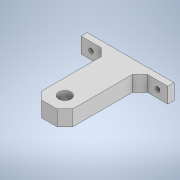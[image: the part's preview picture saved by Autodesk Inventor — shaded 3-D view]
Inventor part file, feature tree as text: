
AUTODESK INVENTOR PART (.ipt)
format: ipt  version: 2022 (Build 260153000, 153)  size: 274,432 bytes
history: native  units: mm
features: sketch x3, extrude x2, hole x2, other x1, chamfer x1
ambient origin geometry x8: Origin, YZ Plane, XZ Plane, XY Plane, X Axis, Y Axis, Z Axis, Center Point
bodies: Body1 (feature_tree)
feature tree (9):
  other  "Sólido1"
  sketch  "Esboço1"  dims[d0=56.0mm d1=10.0mm]
  extrude  "Extrusão1"  Depth=10.0mm
  extrude  "Extrusão2"  Depth=4.0mm TaperAngle=0.0deg
  chamfer  "Chanfro1"  Distance=52.426mm
  hole  "Furo1"  [1 undecoded]
  hole  "Furo2"  [1 undecoded]
  sketch  "Esboço2"  dims[d2=20.0mm d3=4.0mm d4=0.0mm d5=52.426mm d6=0.0mm]
  sketch  "Esboço3"  dims[d7=5.0mm d8=2.0mm d9=45.0deg d10=8.0mm d11=6.0mm d12=4.0mm d13=2.0mm d14=90.0deg d15=8.0mm d16=20.594885mm d17=3.0mm d18=6.0mm d19=4.0mm d20=2.0mm d21=90.0deg d22=8.0mm d23=20.594885mm d24=10.0mm]
note: 2 required parameter values undecoded (feature->parameter linkage not recoverable at this tier; creation-order binding heuristic only, values carry confidence <= 0.55)
